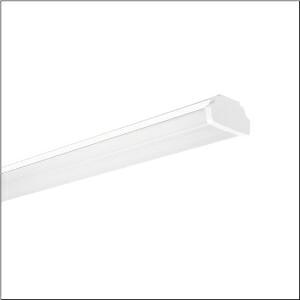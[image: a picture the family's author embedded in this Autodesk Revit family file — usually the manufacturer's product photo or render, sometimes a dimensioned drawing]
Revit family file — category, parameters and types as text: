
# Revit family: modario_r__31_gen_2_53bm812mv4a5c2_e17c
name_source: partatom
category: Lighting Fixtures
units: mm (PartAtom-declared; Revit-internal decimal feet)

## family parameters
Cut with Voids When Loaded = No
Host = Face
Light Source = No
Part Type = Normal
Room Calculation Point = No
Round Connector Dimension = Use Diameter
Shared = No

## types (1)
- --- (1 x LED, 10960 lm, 60.5 W, 4000K)
    Apparent Load = 61 VA
    CIE Flux Codes = 47 80 95 93 100
    Color Rendering = 80
    Color Temperature = 4000K
    Default Elevation = 1800 mm
    Description = Modario® 31 Gen.2, luminaire insert, of sheet steel, coil coated, white, length: 1.495mm, width: 81mm, height: 82mm, 5x system unit, system units: 299mm, LED rated luminous flux: 10.960lm, light colour: 840, control gear: ON/OFF Multilumen, control gear: ECG, with plug, 3-pole, with phase selection, mains connection: 220..240V, AC, 50/60Hz, rated input power: 61W, through-wiring accessed according to module size, primary optical cover: cover, of PMMA, light emission: direct distribution, primary light characteristic: symmetric, protection rating (complete): IP20, protection rating (LED compartment): IP50, insulation class (complete): insulation class I (protective earthing), certification: CE, ENEC, VDE, UKCA, impact resistance: IK03, permissible ambient temperature for indoor applications: -35..+40°C, corresponds to IFS (International Featured Standards) requirements for safety and quality in the food industry, reducing of maximum allowable ambient temperature of 5°C with ceiling mounting, IP40 when using the optional accessory 5TP9018, packaging unit: 1 piece
    Height = 92 mm
    Lamp = 1 x LED
    Lamp Light Flux = 10960 lm
    Lamp Power = 60.5 W
    Lamp count = 1
    Length = 1495 mm
    Luminous efficacy = 181 lm/W
    Manufacturer = Siteco
    ModVariant = No
    Model = 53BM812MV4A5C2
    Mounting Place = Ceiling
    Mounting Type = Pendant
    Number of Poles = 1
    OnlyDefault = Yes
    Power Factor = 1
    Product Name = Modario® 31 Gen.2
    Product group = luminaire insert
    ProductGroupID = 901
    Protection Class = Protection class I
    Protection Degree = IP 20
    RLX_Detail_Level = 1
    RLX_Emergency_Light_Flux = 0 lm
    RLX_Emergency_Type = 0
    RLX_Emergency_Type_DB = No
    RlxData = <blob elided: 40033 chars, md5=75f47d6e>
    Socket = socket
    Standby Power = 0 W
    System Light Flux = 10960 lm
    System Power = 61 W
    Type Comments = factory setting: luminous flux: 100 % | (A | C | E) | 140 mA
    Type Image = l_1319597.jpg
    URL = http://relux.com
    VarID = @adj_010697
    Voltage = 0 V
    Weight = 0.00 kg
    Width = 81 mm

## geometry (parser evidence)
native form markers: Blend x4, Sweep x14
no freeform markers — native parametric forms only
